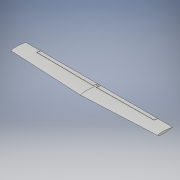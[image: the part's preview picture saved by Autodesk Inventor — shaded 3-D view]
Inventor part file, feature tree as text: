
AUTODESK INVENTOR PART (.ipt)
format: ipt  version: 2019.3 (Build 233278000, 278)  size: 225,792 bytes
history: native  units: mm
features: other x4, sketch x3, plane x2, mirror x2, loft x1, extrude x1
ambient origin geometry x8: Origin, YZ Plane, XZ Plane, XY Plane, X Axis, Y Axis, Z Axis, Center Point
bodies: Solid1 (feature_tree)
feature tree (13):
  sketch  "Sketch1"  dims[d0=0.0mm d1=10.0mm d2=0.0mm d3=10.0mm]
  plane  "Work Plane1"
  loft  "Loft1"
  mirror  "Mirror1"
  plane  "Work Plane2"
  extrude  "Extrusion1"  Depth=10.0mm TaperAngle=0.0deg
  mirror  "Mirror2"
  other  "2D Equation Curve1"
  other  "2D Equation Curve2"
  sketch  "Sketch2"  dims[d4=2000.0mm d5=0.0mm d6=10.0mm]
  other  "2D Equation Curve3"
  other  "2D Equation Curve4"
  sketch  "Sketch3"  dims[d7=0.0mm d8=10.0mm d9=0.0mm d10=90.0deg d11=0.0mm d12=90.0deg d13=500.0mm d14=40.0mm d15=1600.0mm d16=375.5mm d17=395.0mm d18=300.0mm d20=300.0mm d21=5.0mm d22=100.0mm d23=0.0mm]
